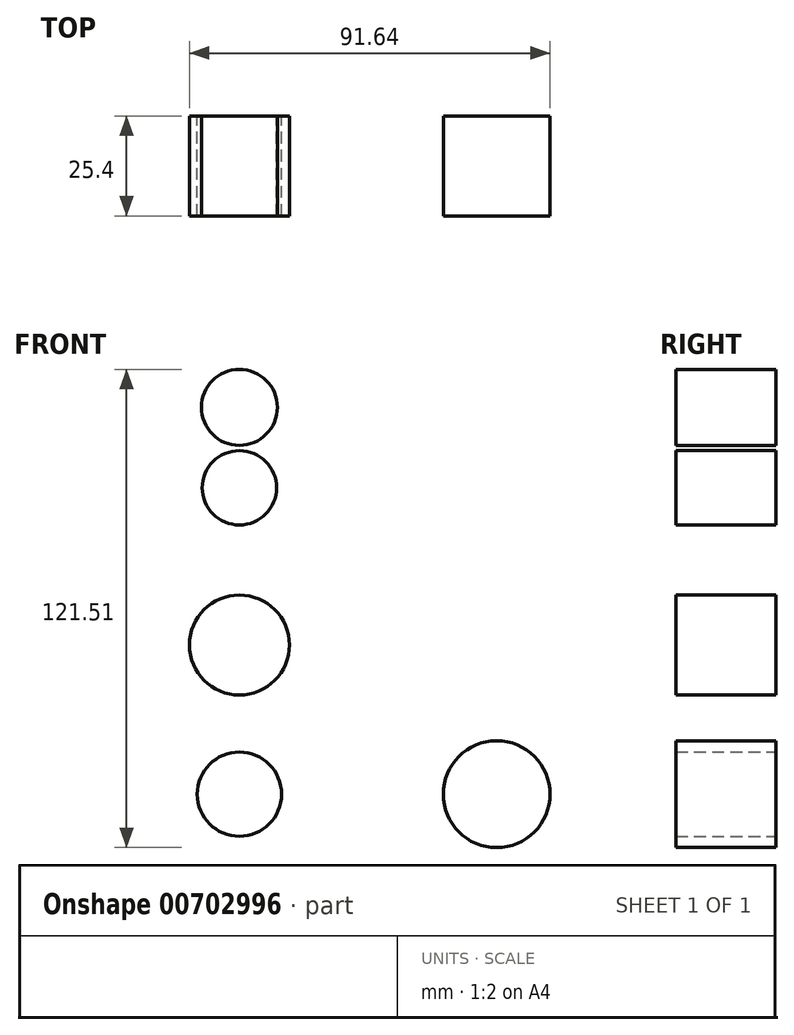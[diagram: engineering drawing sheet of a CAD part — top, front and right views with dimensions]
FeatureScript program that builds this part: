
annotation { "Feature Type Name" : "Feature", "Feature Type Description" : "" }
export const myFeature = defineFeature(function(context is Context, id is Id, definition is map)
    precondition{}
    {
        {
            var Q0;
            Q0=qCreatedBy(makeId("Front.planeOp"),FACE);
            var sketch = newSketch(context, id + "F0", { "sketchPlane" : qUnion([Q0])});
            skLineSegment(sketch, "E0", {"start": v(-22.47, 53.34) * mm, "end": v(-22.47, -48.57) * mm});
            skCircle(sketch, "E1", {"center": v(-22.47, 49.7) * mm, "radius": 9.66 * mm});
            skCircle(sketch, "E2", {"center": v(-22.47, 29.28) * mm, "radius": 9.45 * mm});
            skCircle(sketch, "E3", {"center": v(-22.47, -10.67) * mm, "radius": 12.7 * mm});
            skLineSegment(sketch, "E4", {"start": v(-22.47, -48.57) * mm, "end": v(42.9, -48.57) * mm});
            skCircle(sketch, "E5", {"center": v(-22.47, -48.57) * mm, "radius": 10.7 * mm});
            skCircle(sketch, "E6", {"center": v(42.9, -48.57) * mm, "radius": 13.58 * mm});
            skSolve(sketch);
        }
        {
            var Q0;
            Q0 = qSketchRegion(id + "F0", true);
            extrude(context, id + "F1", {"entities" : qUnion([Q0]), "depth" : 25.4 * mm, "offsetDistance" : 25.4 * mm});
        }
    });
